# Revit family: CL10041-C5A_CLARK CROSS WALL BASIN BATH SET 220MM
name_source: partatom
category: Plumbing Fixtures
revit_build: Autodesk Revit 2015 (Build: 20140606_1530(x64)
units: mm (PartAtom-declared; Revit-internal decimal feet)

## types (2) — shared parameters
Assembly Code = C1030220
CW Connection = Yes
Default Elevation = 900 mm  [stored 2.95276 ft]
Description = CLARK CROSS WALL BASIN BATH SET 220MM
HW Connection = Yes
Manufacturer = GWA Bathrooms & Kitchens
URL = https://www.clark.com.au
Vent Connection = No
WELSRating_ANZRS = 5 Star
Waste Connection = No

## per-type parameters (varying)
| type | Material_Base | Model |
| CLARK CROSS WALL BASIN BATH SET 220MM - Chrome | GWA_Metal-Chrome | CL10041.C5A |
| CLARK CROSS WALL BASIN BATH SET 220MM - Black | GWA-Metal-Black | CL10041.B5A |

note: [stored X ft] marks values corroborated as IEEE doubles in the binary element streams (Revit-internal decimal feet)

## geometry (parser evidence)
native form markers: Sweep x2
no freeform markers — native parametric forms only
